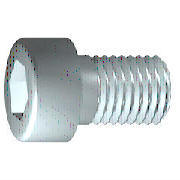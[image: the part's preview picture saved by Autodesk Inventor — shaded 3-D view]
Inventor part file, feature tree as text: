
AUTODESK INVENTOR PART (.ipt)
format: ipt  version: 2013 (Build 170138000, 138)  size: 182,272 bytes
history: native  units: mm (DEFAULTED — no unit token found)
features: sketch x2, extrude x1, plane x1, fillet x1
ambient origin geometry x7: Origin, YZ Plane, XY Plane, X Axis, Y Axis, Z Axis, Center Point
bodies: Solid1 (feature_tree), Body (feature_tree)
feature tree (5):
  extrude  "Slot"  Depth=0.306825mm
  plane  "Work Plane1"
  fillet  "Fillet2"  Radius=3.0mm
  sketch  "Sketch1"  dims[d1=18.0mm d2=0.306825mm d3=3.0mm]
  sketch  "Sketch2"  dims[d4=1.5mm d5=60.0deg d6=3.0mm d7=3.0mm d8=2.886751mm d9=5.5mm d10=90.0deg d11=10.0mm d12=0.0mm d13=18.0mm d14=0.0mm d15=0.306725mm d16=0.306725mm d17=0.3mm d19=0.0mm d26=30.0mm d27=45.0deg d28=0.0mm d29=0.0mm d30=0.1mm]
